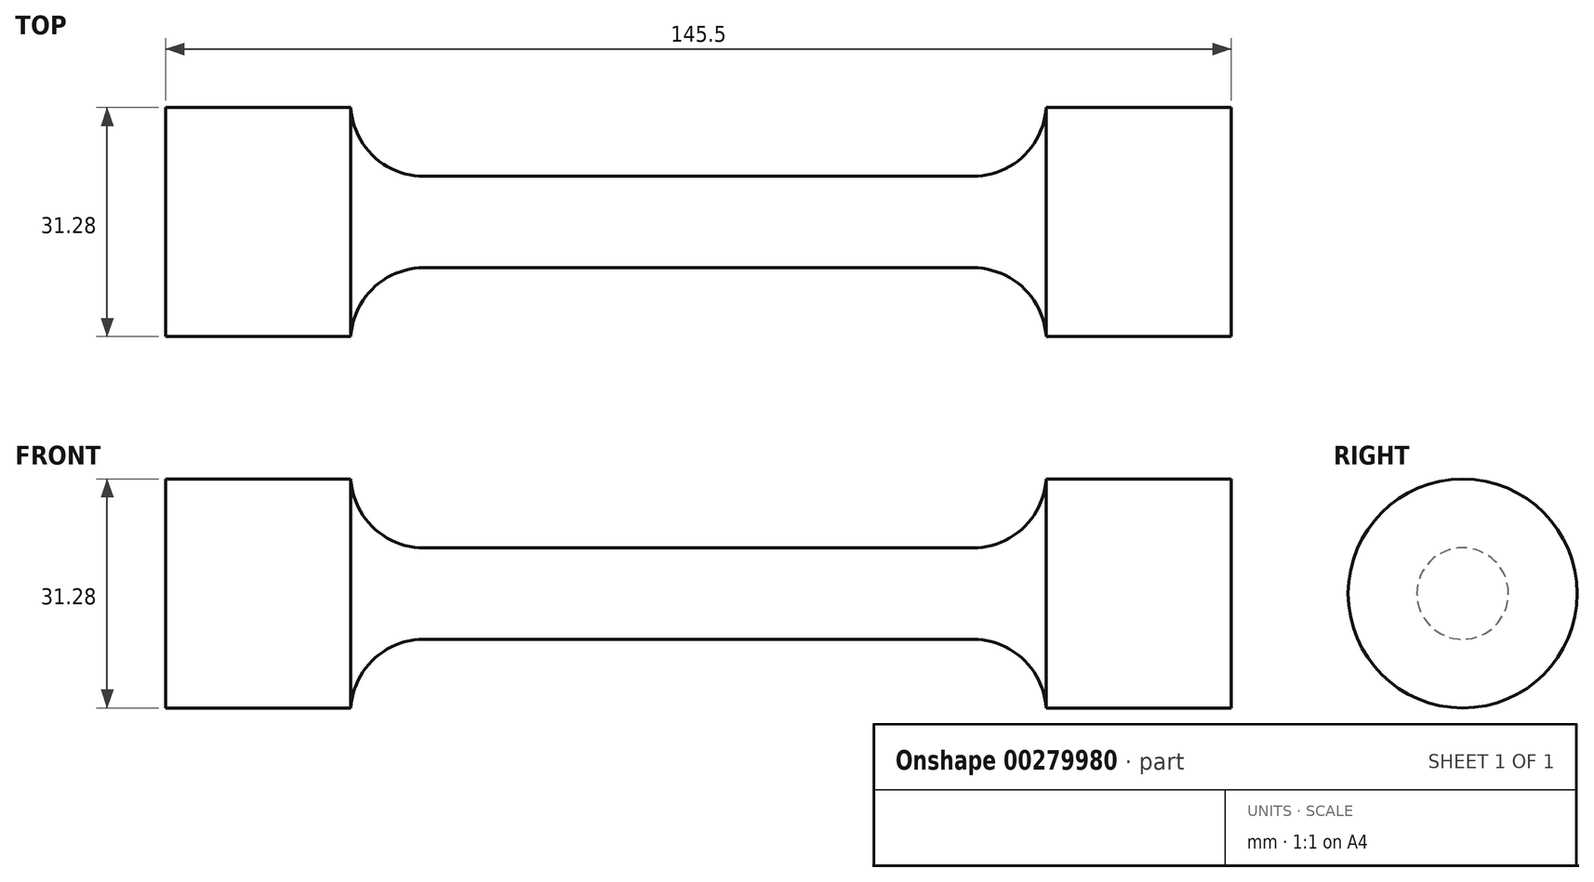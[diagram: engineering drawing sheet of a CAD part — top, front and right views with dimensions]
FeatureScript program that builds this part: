
annotation { "Feature Type Name" : "Feature", "Feature Type Description" : "" }
export const myFeature = defineFeature(function(context is Context, id is Id, definition is map)
    precondition{}
    {
        {
            var Q0;
            Q0=qCreatedBy(makeId("Front.planeOp"),FACE);
            var sketch = newSketch(context, id + "F0", { "sketchPlane" : qUnion([Q0])});
            skLineSegment(sketch, "E0", {"start": v(0, 6.25) * mm, "end": v(37.5, 6.25) * mm});
            skArc(sketch, "E1", {"start": v(37.5, 6.25) * mm, "mid": v(44.35, 8.97) * mm, "end": v(47.48, 15.64) * mm});
            skLineSegment(sketch, "E2", {"start": v(47.48, 15.64) * mm, "end": v(72.75, 15.64) * mm});
            skLineSegment(sketch, "E3", {"start": v(72.75, 15.64) * mm, "end": v(72.75, 0) * mm});
            skLineSegment(sketch, "E4.MirrorCS", {"start": v(0, 6.25) * mm, "end": v(-37.5, 6.25) * mm});
            skArc(sketch, "E5.MirrorCS", {"start": v(-37.5, 6.25) * mm, "mid": v(-44.35, 8.97) * mm, "end": v(-47.48, 15.64) * mm});
            skLineSegment(sketch, "E6.MirrorCS", {"start": v(-47.48, 15.64) * mm, "end": v(-72.75, 15.64) * mm});
            skLineSegment(sketch, "E7.MirrorCS", {"start": v(-72.75, 15.64) * mm, "end": v(-72.75, 0) * mm});
            skLineSegment(sketch, "E8", {"start": v(-72.75, 0) * mm, "end": v(72.75, 0) * mm});
            skSolve(sketch);
        }
        {
            var Q0;
            Q0=makeQuery(id+"F0.imprint","IMPRINT",FACE,{"disambiguationData":[TD([[makeQuery(id+"F0.imprint","IMPRINT",EDGE,{"derivedFrom":sQuery(id+"F0.wireOp",EDGE,"E0")}),-1.0]])]});
            var Q1;
            Q1=sQuery(id+"F0.wireOp",EDGE,"E8");
            revolve(context, id + "F1", {"entities" : qUnion([Q0]), "axis" : qUnion([Q1]), "revolveType" : RevolveType.FULL});
        }
    });
